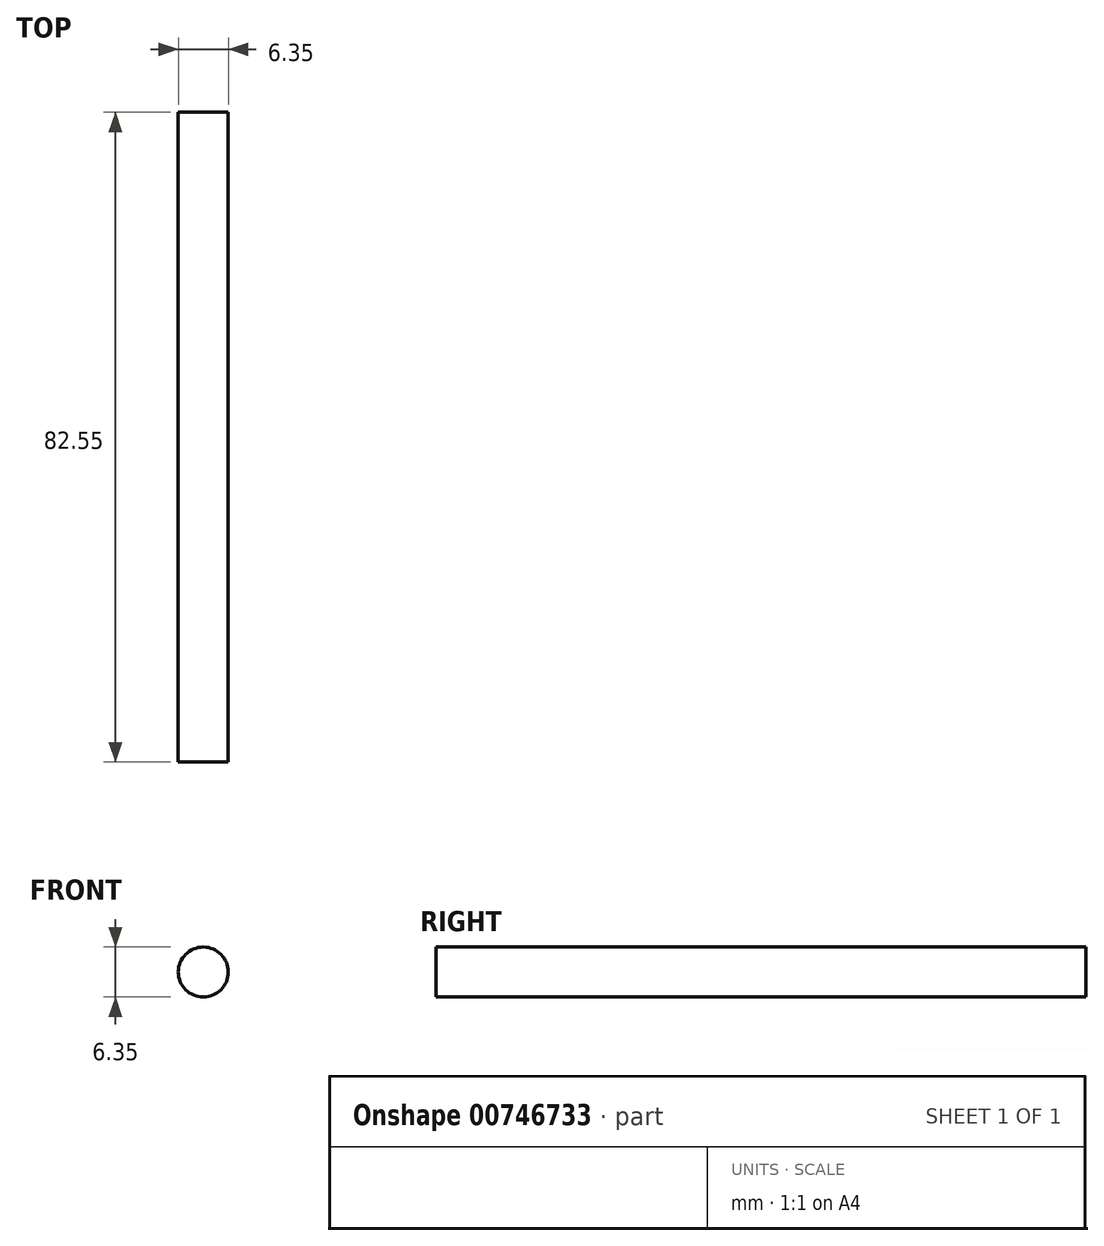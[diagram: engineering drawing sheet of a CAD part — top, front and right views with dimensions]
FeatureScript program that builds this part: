
annotation { "Feature Type Name" : "Feature", "Feature Type Description" : "" }
export const myFeature = defineFeature(function(context is Context, id is Id, definition is map)
    precondition{}
    {
        {
            var Q0;
            Q0=qCreatedBy(makeId("Front.planeOp"),FACE);
            var sketch = newSketch(context, id + "F0", { "sketchPlane" : qUnion([Q0])});
            skCircle(sketch, "E0", {"center": v(-13.8, -16.8) * mm, "radius": 3.17 * mm});
            skSolve(sketch);
        }
        {
            var Q0;
            Q0 = qSketchRegion(id + "F0", true);
            extrude(context, id + "F1", {"entities" : qUnion([Q0]), "depth" : 82.55 * mm, "offsetDistance" : 25.4 * mm});
        }
    });
